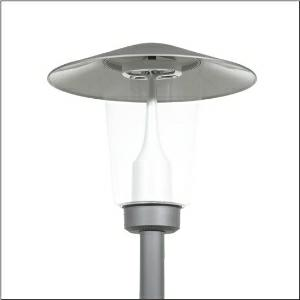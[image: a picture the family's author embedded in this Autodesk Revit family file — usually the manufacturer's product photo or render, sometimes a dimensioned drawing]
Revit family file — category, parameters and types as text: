
# Revit family: pilzleuchte_iq___st1_2a_5xa5235mf14h_7035
name_source: partatom
category: Lighting Fixtures
units: mm (PartAtom-declared; Revit-internal decimal feet)

## family parameters
Cut with Voids When Loaded = No
Host = Face
Light Source = No
Part Type = Normal
Room Calculation Point = No
Round Connector Dimension = Use Diameter
Shared = No

## types (1)
- --- (1 x LED, 1550 lm, 11.8 W, 2700K)
    Apparent Load = 12 VA
    CIE Flux Codes = 24 61 93 98 100
    Color Rendering = 70
    Color Temperature = 2700K
    Default Elevation = 1800 mm
    Description = Mushroom Luminaire iQ, mast luminaire, Module 540 iQ-SR, primary light control with 3 zone facetted reflector, of plastic, silver coated, highly specular, structured, primary optical cover: cover, of PMMA, transparent, light distribution: ST1.2a, light emission: direct distribution, primary light characteristic: asymmetric, installation type: post-top, LED, High Power LED, rated luminous flux: 1.550lm, luminous efficacy: 131lm/W, light colour: 727, colour temperature: 2700K, control gear: iQ Street-Remote, control: pre-setting: logarithmic dimming characteristic, Street-Remote, Auto-Match, Temp-Guard, Lumen-Switch, Night-Set, Smart-Wire, Light-Fading, Desk-Remote (wireless, voltage-free reading and setting of iQ features in the workshop via application-optimized NFC function/RFID function), optimised constant luminous flux control (CLO 2.0), with terminal, 6-pole, max. 2.5mm², mains connection: 230..240V, AC, 50/60Hz, start of lifetime: 12W, end of service life: 12W, reduction: 6W, luminaire housing, upper part, of glass-fibre reinforced polyester, coated, Siteco® metallic grey (DB 702S), diameter: 650mm, height: 586mm, spigot size: d x l = 76 x 70mm (post-top) | with reducer (optional accessory) 60 x 70mm, mounting height: 3..5m, post-top mast mounting element, of diecast aluminium, coated, Siteco® metallic grey (DB 702S), Module 540 iQ-SR, traffic white (RAL 9016), equipment: standard, protection rating (complete): IP65, insulation class (complete): insulation class II (safety insulation), certification: CE, ENEC, VDE, packaging unit: 1 piece

Light Distribution: ST1.2a
    Height = 586 mm
    Lamp = 1 x LED
    Lamp Light Flux = 1550 lm
    Lamp Power = 11.8 W
    Lamp count = 1
    Length = 650 mm
    Luminous efficacy = 131 lm/W
    Manufacturer = Siteco
    ModVariant = No
    Model = 5XA5235MF14H
    Number of Poles = 1
    OnlyDefault = Yes
    Power Factor = 1
    Product Name = Pilzleuchte iQ | ST1.2a
    Product group = mast luminaire | pylon top
    ProductGroupID = 6100
    Protection Class = Protection class II
    Protection Degree = IP 65
    RLX_Detail_Level = 1
    RLX_Emergency_Light_Flux = 0 lm
    RLX_Emergency_Type = 0
    RLX_Emergency_Type_DB = No
    RlxData = <blob elided: 123529 chars, md5=96b430ca>
    Socket = socket
    Standby Power = 0 W
    System Light Flux = 1550 lm
    System Power = 12 W
    Type Comments = factory setting: luminous flux: 100 % | dim-lin: 254 | 472 mA
    Type Image = l_1006077.jpg
    URL = http://relux.com
    VarID = @adj_153478
    Voltage = 0 V
    Weight = 0.00 kg
    Width = 0 mm  [stored 0 ft]

note: [stored X ft] marks values corroborated as IEEE doubles in the binary element streams (Revit-internal decimal feet)

## geometry (parser evidence)
native form markers: Blend x4, Sweep x9
no freeform markers — native parametric forms only
